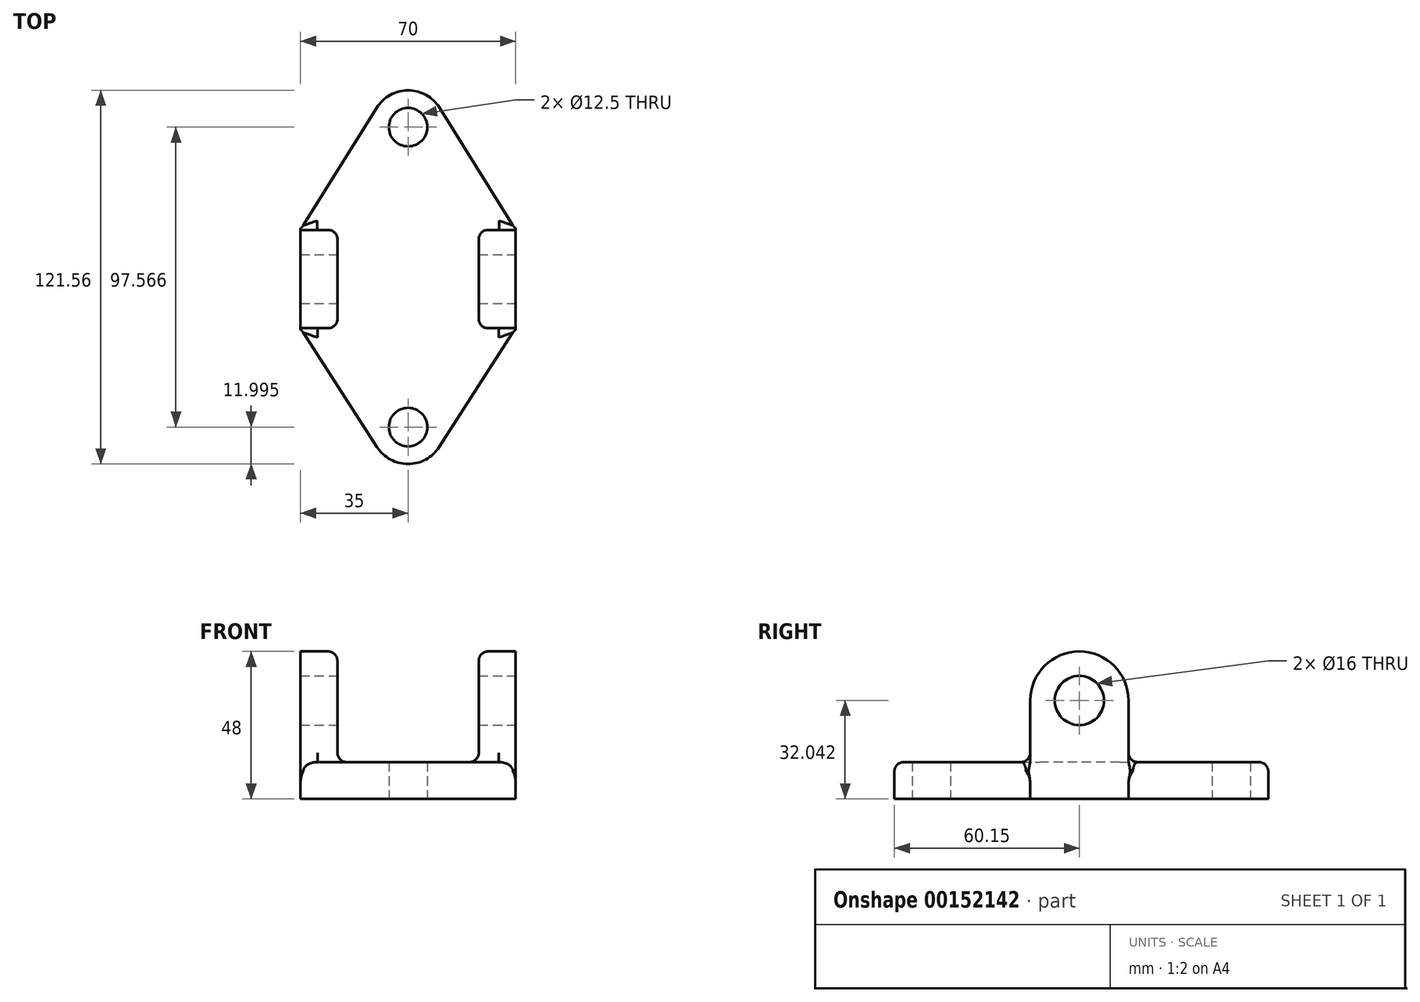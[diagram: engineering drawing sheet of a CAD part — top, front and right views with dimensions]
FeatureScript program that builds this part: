
annotation { "Feature Type Name" : "Feature", "Feature Type Description" : "" }
export const myFeature = defineFeature(function(context is Context, id is Id, definition is map)
    precondition{}
    {
        {
            var Q0;
            Q0=qCreatedBy(makeId("Right.planeOp"),FACE);
            var sketch = newSketch(context, id + "F0", { "sketchPlane" : qUnion([Q0])});
            skLineSegment(sketch, "E0", {"start": v(-16, 0) * mm, "end": v(-16, 32) * mm});
            skLineSegment(sketch, "E1", {"start": v(-16, 0) * mm, "end": v(16, 0) * mm});
            skLineSegment(sketch, "E2", {"start": v(16, 0) * mm, "end": v(16, 32) * mm});
            skCircle(sketch, "E3", {"center": v(0, 32) * mm, "radius": 6 * mm});
            skArc(sketch, "E4", {"start": v(16, 32) * mm, "mid": v(0, 48) * mm, "end": v(-16, 32) * mm});
            skSolve(sketch);
        }
        {
            var Q0;
            Q0=qSketchRegion(id+"F0",true);
            extrude(context, id + "F1", {"entities" : qUnion([Q0]), "oppositeDirection" : true, "depth" : 12 * mm});
        }
        {
            var Q0;
            Q0=qCreatedBy(makeId("Top.planeOp"),FACE);
            var sketch = newSketch(context, id + "F2", { "sketchPlane" : qUnion([Q0])});
            skPoint(sketch, "E5.0", {"position": v(-12, 16) * mm});
            skPoint(sketch, "E6.0", {"position": v(-12, -16) * mm});
            skCircle(sketch, "E7", {"center": v(23, 49.41) * mm, "radius": 6.25 * mm});
            skArc(sketch, "E8", {"start": v(33.18, 55.77) * mm, "mid": v(23, 61.41) * mm, "end": v(12.82, 55.77) * mm});
            skLineSegment(sketch, "E9", {"start": v(33.18, 55.77) * mm, "end": v(58, 16) * mm});
            skPoint(sketch, "E10", {"position": v(-12, 0) * mm});
            skPoint(sketch, "E11", {"position": v(58, 0) * mm});
            skLineSegment(sketch, "E12", {"start": v(58, 0) * mm, "end": v(58, -16) * mm});
            skLineSegment(sketch, "E13", {"start": v(58, -16) * mm, "end": v(58, 16) * mm});
            skPoint(sketch, "E14", {"position": v(23, 0) * mm});
            skLineSegment(sketch, "E15", {"start": v(23, 74.76) * mm, "end": v(23, -48.15) * mm, "construction": true});
            skLineSegment(sketch, "E16", {"start": v(-12, 16) * mm, "end": v(12.82, 55.77) * mm});
            skCircle(sketch, "E17", {"center": v(23, -48.15) * mm, "radius": 6.25 * mm});
            skArc(sketch, "E18", {"start": v(12.91, -54.66) * mm, "mid": v(23, -60.15) * mm, "end": v(33.09, -54.66) * mm});
            skLineSegment(sketch, "E19", {"start": v(58, -16) * mm, "end": v(33.09, -54.66) * mm});
            skLineSegment(sketch, "E20", {"start": v(12.91, -54.66) * mm, "end": v(-12, -16) * mm});
            skLineSegment(sketch, "E21", {"start": v(-12, -16) * mm, "end": v(-12, 16) * mm});
            skSolve(sketch);
        }
        {
            var Q0;
            Q0=qSketchRegion(id+"F2",true);
            extrude(context, id + "F3", {"entities" : qUnion([Q0]), "operationType" : NewBodyOperationType.ADD, "depth" : 12 * mm});
        }
        {
            var Q0;
            Q0=makeQuery(id+"F3.opExtrude","SWEPT_FACE",FACE,{"disambiguationData":[OSD([sQuery(id+"F2.wireOp",EDGE,"E13")])]});
            var sketch = newSketch(context, id + "F4", { "sketchPlane" : qUnion([Q0])});
            skLineSegment(sketch, "E22.0.0", {"start": v(-16, 0) * mm, "end": v(-16, 12) * mm});
            skLineSegment(sketch, "E22.0.1", {"start": v(-16, 12) * mm, "end": v(-16, 32) * mm});
            skArc(sketch, "E22.0.2", {"start": v(-16, 32) * mm, "mid": v(0, 48) * mm, "end": v(16, 32) * mm});
            skLineSegment(sketch, "E22.0.3", {"start": v(16, 32) * mm, "end": v(16, 12) * mm});
            skLineSegment(sketch, "E22.0.4", {"start": v(16, 12) * mm, "end": v(16, 0) * mm});
            skLineSegment(sketch, "E22.0.5", {"start": v(16, 0) * mm, "end": v(-16, 0) * mm});
            skCircle(sketch, "E23.0", {"center": v(0, 32) * mm, "radius": 6 * mm});
            skSolve(sketch);
        }
        {
            var Q0;
            Q0=qSketchRegion(id+"F4",true);
            extrude(context, id + "F5", {"entities" : qUnion([Q0]), "operationType" : NewBodyOperationType.ADD, "oppositeDirection" : true, "depth" : 12 * mm});
        }
        {
            var Q0;
            Q0=makeQuery(id+"F3.opExtrude","CAP_EDGE",EDGE,{"disambiguationData":[OSD([sQuery(id+"F2.wireOp",EDGE,"E19")])],"isStart":false});
            var Q1;
            Q1=makeQuery(id+"F3.opExtrude","CAP_EDGE",EDGE,{"disambiguationData":[OSD([sQuery(id+"F2.wireOp",EDGE,"E9")])],"isStart":false});
            var Q2;
            Q2=makeQuery(id+"F5.opExtrude","CAP_EDGE",EDGE,{"disambiguationData":[OSD([sQuery(id+"F4.wireOp",EDGE,"E22.0.2")])],"isStart":false});
            var Q3;
            Q3=makeQuery(id+"F1.opExtrude","CAP_EDGE",EDGE,{"disambiguationData":[OSD([sQuery(id+"F0.wireOp",EDGE,"E4")])],"isStart":true});
            fillet(context, id + "F6", {"entities" : qUnion([Q0, Q1, Q2, Q3]), "radius" : 3 * mm, "tangentPropagation" : true, "allowEdgeOverflow" : false});
        }
        {
            var Q0;
            Q0=makeQuery(id+"F5.boolean.opBoolean","INTERSECT",EDGE,{"derivedFrom":[makeQuery(id+"F3.opExtrude","CAP_FACE",FACE,{"disambiguationData":[OSD([sQuery(id+"F2.wireOp",EDGE,"E7"),sQuery(id+"F2.wireOp",EDGE,"E8"),sQuery(id+"F2.wireOp",EDGE,"E9"),sQuery(id+"F2.wireOp",EDGE,"E13"),sQuery(id+"F2.wireOp",EDGE,"E16"),sQuery(id+"F2.wireOp",EDGE,"E17"),sQuery(id+"F2.wireOp",EDGE,"E18"),sQuery(id+"F2.wireOp",EDGE,"E19"),sQuery(id+"F2.wireOp",EDGE,"E20"),sQuery(id+"F2.wireOp",EDGE,"E21")])],"isStart":false}),makeQuery(id+"F5.opExtrude","SWEPT_FACE",FACE,{"disambiguationData":[OSD([sQuery(id+"F4.wireOp",EDGE,"E22.0.0"),sQuery(id+"F4.wireOp",EDGE,"E22.0.1")])]})]});
            var Q1;
            Q1=makeQuery(id+"F3.boolean.opBoolean","INTERSECT",EDGE,{"derivedFrom":[makeQuery(id+"F1.opExtrude","SWEPT_FACE",FACE,{"disambiguationData":[OSD([sQuery(id+"F0.wireOp",EDGE,"E0")])]}),makeQuery(id+"F3.opExtrude","CAP_FACE",FACE,{"disambiguationData":[OSD([sQuery(id+"F2.wireOp",EDGE,"E7"),sQuery(id+"F2.wireOp",EDGE,"E8"),sQuery(id+"F2.wireOp",EDGE,"E9"),sQuery(id+"F2.wireOp",EDGE,"E13"),sQuery(id+"F2.wireOp",EDGE,"E16"),sQuery(id+"F2.wireOp",EDGE,"E17"),sQuery(id+"F2.wireOp",EDGE,"E18"),sQuery(id+"F2.wireOp",EDGE,"E19"),sQuery(id+"F2.wireOp",EDGE,"E20"),sQuery(id+"F2.wireOp",EDGE,"E21")])],"isStart":false})]});
            fillet(context, id + "F7", {"entities" : qUnion([Q0, Q1]), "radius" : 3 * mm, "tangentPropagation" : true, "allowEdgeOverflow" : false});
        }
        {
            var Q0;
            Q0=makeQuery(id+"F4.imprint","IMPRINT",FACE,{"disambiguationData":[TD([[makeQuery(id+"F4.imprint","IMPRINT",EDGE,{"derivedFrom":sQuery(id+"F4.wireOp",EDGE,"E22.0.1")}),-1.0]])]});
            var sketch = newSketch(context, id + "F8", { "sketchPlane" : qUnion([Q0])});
            skCircle(sketch, "E24", {"center": v(0, 32.04) * mm, "radius": 8 * mm});
            skLineSegment(sketch, "E25", {"start": v(-12.88, 17) * mm, "end": v(13.25, 17) * mm});
            skLineSegment(sketch, "E26", {"start": v(13.25, 17) * mm, "end": v(10.48, 42.4) * mm});
            skLineSegment(sketch, "E27", {"start": v(10.48, 42.4) * mm, "end": v(-7.83, 42.4) * mm});
            skLineSegment(sketch, "E28", {"start": v(-7.83, 42.4) * mm, "end": v(-12.88, 17) * mm});
            skSolve(sketch);
        }
        {
            var Q0;
            Q0=makeQuery(id+"F8.imprint","IMPRINT",FACE,{"disambiguationData":[TD([[makeQuery(id+"F8.imprint","IMPRINT",EDGE,{"derivedFrom":sQuery(id+"F8.wireOp",EDGE,"E24")}),1.0]])]});
            extrude(context, id + "F9", {"entities" : qUnion([Q0]), "operationType" : NewBodyOperationType.REMOVE, "endBound" : BoundingType.THROUGH_ALL, "oppositeDirection" : true, "depth" : 25 * mm});
        }
    });
